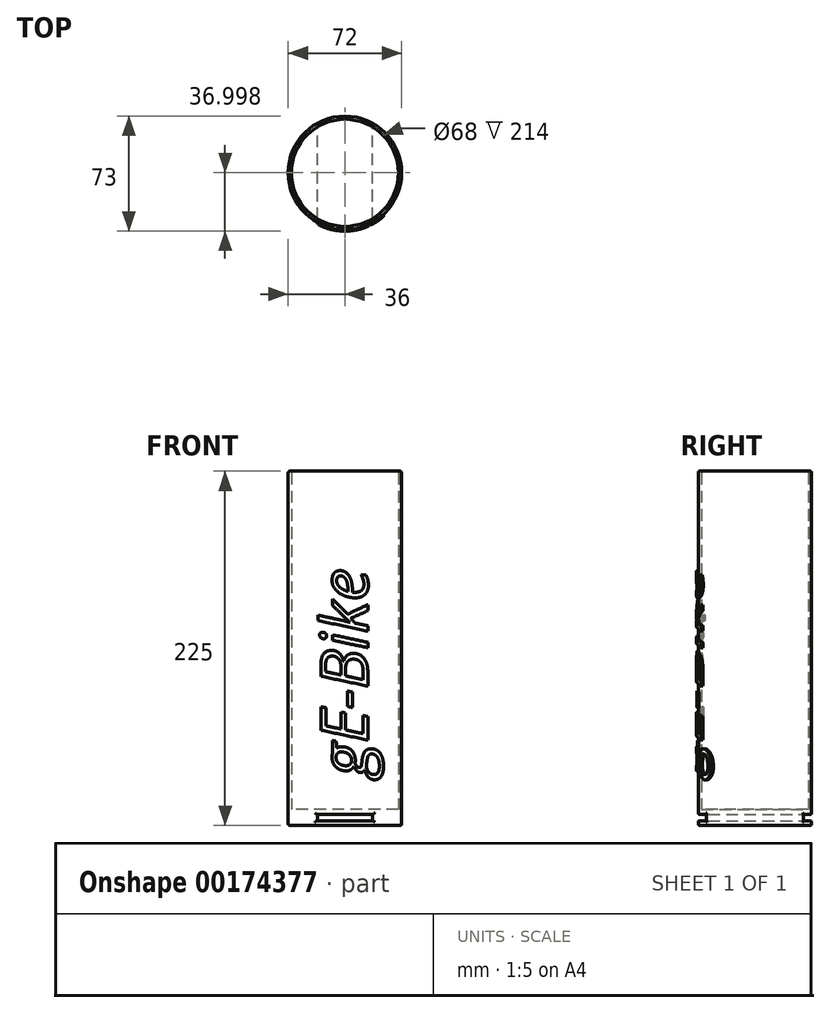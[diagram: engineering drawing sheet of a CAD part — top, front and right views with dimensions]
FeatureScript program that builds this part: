
annotation { "Feature Type Name" : "Feature", "Feature Type Description" : "" }
export const myFeature = defineFeature(function(context is Context, id is Id, definition is map)
    precondition{}
    {
        {
            var Q0;
            Q0=qCreatedBy(makeId("Top.planeOp"),FACE);
            var sketch = newSketch(context, id + "F0", { "sketchPlane" : qUnion([Q0])});
            skCircle(sketch, "E0.0", {"center": v(0, -2.8) * mm, "radius": 36 * mm});
            skLineSegment(sketch, "E1", {"start": v(0, 33.2) * mm, "end": v(0, -38.8) * mm});
            skLineSegment(sketch, "E2", {"start": v(0, -2.8) * mm, "end": v(-36, -2.8) * mm});
            skLineSegment(sketch, "E3", {"start": v(0, -2.8) * mm, "end": v(36, -2.8) * mm});
            skSolve(sketch);
        }
        {
            var Q0;
            Q0 = qSketchRegion(id + "F0", true);
            var Q1;
            Q1=makeQuery(id+"F0.imprint","IMPRINT",FACE,{"disambiguationData":[TD([[makeQuery(id+"F0.imprint","IMPRINT",EDGE,{"derivedFrom":sQuery(id+"F0.wireOp",EDGE,"E0.0")}),1.0]])]});
            extrude(context, id + "F1", {"entities" : qUnion([Q0, Q1]), "depth" : 10 * mm});
        }
        {
            var Q0;
            Q0=makeQuery(id+"F1.opExtrude","CAP_FACE",FACE,{"disambiguationData":[OSD([sQuery(id+"F0.wireOp",EDGE,"E0.0")])],"isStart":false});
            var sketch = newSketch(context, id + "F2", { "sketchPlane" : qUnion([Q0])});
            skCircle(sketch, "E4.0", {"center": v(0, -2.8) * mm, "radius": 34 * mm});
            skSolve(sketch);
        }
        {
            var Q0;
            Q0=makeQuery(id+"F2.imprint","IMPRINT",FACE,{"disambiguationData":[TD([[makeQuery(id+"F2.imprint","IMPRINT",EDGE,{"derivedFrom":sQuery(id+"F2.wireOp",EDGE,"E4.0")}),-1.0]])]});
            extrude(context, id + "F3", {"entities" : qUnion([Q0]), "operationType" : NewBodyOperationType.ADD, "depth" : 215 * mm});
        }
        {
            var Q0;
            Q0=qCreatedBy(makeId("Front.planeOp"),FACE);
            var sketch = newSketch(context, id + "F4", { "sketchPlane" : qUnion([Q0])});
            skLineSegment(sketch, "E5", {"start": v(-42.08, 0) * mm, "end": v(47.5, 0) * mm});
            skLineSegment(sketch, "E6.0", {"start": v(-17.5, 3) * mm, "end": v(17.5, 3) * mm});
            skLineSegment(sketch, "E7.0", {"start": v(-17.5, 7) * mm, "end": v(17.5, 7) * mm});
            skLineSegment(sketch, "E8.0", {"start": v(17.5, 3) * mm, "end": v(17.5, 7) * mm});
            skLineSegment(sketch, "E9.0", {"start": v(-17.5, 3) * mm, "end": v(-17.5, 7) * mm});
            skSolve(sketch);
        }
        {
            var Q0;
            Q0 = qSketchRegion(id + "F4", true);
            extrude(context, id + "F5", {"entities" : qUnion([Q0]), "operationType" : NewBodyOperationType.REMOVE, "endBound" : BoundingType.THROUGH_ALL, "depth" : 44.2 * mm, "hasSecondDirection" : true, "secondDirectionOppositeDirection" : true, "secondDirectionDepth" : 36.8 * mm});
        }
        {
            var Q0;
            Q0=makeQuery(id+"F3.opExtrude","CAP_EDGE",EDGE,{"disambiguationData":[OSD([sQuery(id+"F2.wireOp",EDGE,"E4.0")])],"isStart":false});
            var Q1;
            Q1=makeQuery(id+"F3.opExtrude","CAP_EDGE",EDGE,{"disambiguationData":[OSD([sQuery(id+"F0.wireOp",EDGE,"E0.0")])],"isStart":false});
            var Q2;
            Q2=makeQuery(id+"F1.opExtrude","CAP_EDGE",EDGE,{"disambiguationData":[OSD([sQuery(id+"F0.wireOp",EDGE,"E0.0")])],"isStart":true});
            var Q3;
            {var subQ0=sQuery(id+"F0.wireOp",EDGE,"E0.0");Q3=makeQuery(id+"F5.boolean.opBoolean","INTERSECT",EDGE,{"disambiguationData":[OD(0.0)],"derivedFrom":[makeQuery(id+"F3.boolean.opBoolean","MERGE",FACE,{"derivedFrom":[makeQuery(id+"F1.opExtrude","SWEPT_FACE",FACE,{"disambiguationData":[OSD([subQ0])]}),makeQuery(id+"F3.opExtrude","SWEPT_FACE",FACE,{"disambiguationData":[OSD([subQ0])]})]}),makeQuery(id+"F5.opExtrude","SWEPT_FACE",FACE,{"disambiguationData":[OSD([sQuery(id+"F4.wireOp",EDGE,"E7.0")])]})]});}
            var Q4;
            {var subQ0=sQuery(id+"F0.wireOp",EDGE,"E0.0");Q4=makeQuery(id+"F5.boolean.opBoolean","INTERSECT",EDGE,{"disambiguationData":[OD(0.0)],"derivedFrom":[makeQuery(id+"F3.boolean.opBoolean","MERGE",FACE,{"derivedFrom":[makeQuery(id+"F1.opExtrude","SWEPT_FACE",FACE,{"disambiguationData":[OSD([subQ0])]}),makeQuery(id+"F3.opExtrude","SWEPT_FACE",FACE,{"disambiguationData":[OSD([subQ0])]})]}),makeQuery(id+"F5.opExtrude","SWEPT_FACE",FACE,{"disambiguationData":[OSD([sQuery(id+"F4.wireOp",EDGE,"E9.0")])]})]});}
            var Q5;
            {var subQ0=sQuery(id+"F0.wireOp",EDGE,"E0.0");Q5=makeQuery(id+"F5.boolean.opBoolean","INTERSECT",EDGE,{"disambiguationData":[OD(0.0)],"derivedFrom":[makeQuery(id+"F3.boolean.opBoolean","MERGE",FACE,{"derivedFrom":[makeQuery(id+"F1.opExtrude","SWEPT_FACE",FACE,{"disambiguationData":[OSD([subQ0])]}),makeQuery(id+"F3.opExtrude","SWEPT_FACE",FACE,{"disambiguationData":[OSD([subQ0])]})]}),makeQuery(id+"F5.opExtrude","SWEPT_FACE",FACE,{"disambiguationData":[OSD([sQuery(id+"F4.wireOp",EDGE,"E6.0")])]})]});}
            var Q6;
            {var subQ0=sQuery(id+"F0.wireOp",EDGE,"E0.0");Q6=makeQuery(id+"F5.boolean.opBoolean","INTERSECT",EDGE,{"disambiguationData":[OD(0.0)],"derivedFrom":[makeQuery(id+"F3.boolean.opBoolean","MERGE",FACE,{"derivedFrom":[makeQuery(id+"F1.opExtrude","SWEPT_FACE",FACE,{"disambiguationData":[OSD([subQ0])]}),makeQuery(id+"F3.opExtrude","SWEPT_FACE",FACE,{"disambiguationData":[OSD([subQ0])]})]}),makeQuery(id+"F5.opExtrude","SWEPT_FACE",FACE,{"disambiguationData":[OSD([sQuery(id+"F4.wireOp",EDGE,"E8.0")])]})]});}
            var Q7;
            {var subQ0=sQuery(id+"F0.wireOp",EDGE,"E0.0");Q7=makeQuery(id+"F5.boolean.opBoolean","INTERSECT",EDGE,{"disambiguationData":[OD(1.0)],"derivedFrom":[makeQuery(id+"F3.boolean.opBoolean","MERGE",FACE,{"derivedFrom":[makeQuery(id+"F1.opExtrude","SWEPT_FACE",FACE,{"disambiguationData":[OSD([subQ0])]}),makeQuery(id+"F3.opExtrude","SWEPT_FACE",FACE,{"disambiguationData":[OSD([subQ0])]})]}),makeQuery(id+"F5.opExtrude","SWEPT_FACE",FACE,{"disambiguationData":[OSD([sQuery(id+"F4.wireOp",EDGE,"E7.0")])]})]});}
            var Q8;
            {var subQ0=sQuery(id+"F0.wireOp",EDGE,"E0.0");Q8=makeQuery(id+"F5.boolean.opBoolean","INTERSECT",EDGE,{"disambiguationData":[OD(1.0)],"derivedFrom":[makeQuery(id+"F3.boolean.opBoolean","MERGE",FACE,{"derivedFrom":[makeQuery(id+"F1.opExtrude","SWEPT_FACE",FACE,{"disambiguationData":[OSD([subQ0])]}),makeQuery(id+"F3.opExtrude","SWEPT_FACE",FACE,{"disambiguationData":[OSD([subQ0])]})]}),makeQuery(id+"F5.opExtrude","SWEPT_FACE",FACE,{"disambiguationData":[OSD([sQuery(id+"F4.wireOp",EDGE,"E9.0")])]})]});}
            var Q9;
            {var subQ0=sQuery(id+"F0.wireOp",EDGE,"E0.0");Q9=makeQuery(id+"F5.boolean.opBoolean","INTERSECT",EDGE,{"disambiguationData":[OD(1.0)],"derivedFrom":[makeQuery(id+"F3.boolean.opBoolean","MERGE",FACE,{"derivedFrom":[makeQuery(id+"F1.opExtrude","SWEPT_FACE",FACE,{"disambiguationData":[OSD([subQ0])]}),makeQuery(id+"F3.opExtrude","SWEPT_FACE",FACE,{"disambiguationData":[OSD([subQ0])]})]}),makeQuery(id+"F5.opExtrude","SWEPT_FACE",FACE,{"disambiguationData":[OSD([sQuery(id+"F4.wireOp",EDGE,"E6.0")])]})]});}
            var Q10;
            {var subQ0=sQuery(id+"F0.wireOp",EDGE,"E0.0");Q10=makeQuery(id+"F5.boolean.opBoolean","INTERSECT",EDGE,{"disambiguationData":[OD(1.0)],"derivedFrom":[makeQuery(id+"F3.boolean.opBoolean","MERGE",FACE,{"derivedFrom":[makeQuery(id+"F1.opExtrude","SWEPT_FACE",FACE,{"disambiguationData":[OSD([subQ0])]}),makeQuery(id+"F3.opExtrude","SWEPT_FACE",FACE,{"disambiguationData":[OSD([subQ0])]})]}),makeQuery(id+"F5.opExtrude","SWEPT_FACE",FACE,{"disambiguationData":[OSD([sQuery(id+"F4.wireOp",EDGE,"E8.0")])]})]});}
            fillet(context, id + "F6", {"entities" : qUnion([Q0, Q1, Q2, Q3, Q4, Q5, Q6, Q7, Q8, Q9, Q10]), "radius" : 1 * mm, "tangentPropagation" : true, "allowEdgeOverflow" : false});
        }
        {
            var Q0;
            Q0=qCreatedBy(makeId("Front.planeOp"),FACE);
            cPlane(context, id + "F7", {"entities" : qUnion([Q0]), "cplaneType" : CPlaneType.OFFSET, "offset" : 40 * mm, "width" : 150 * mm, "height" : 150 * mm});
        }
        {
            var Q0;
            Q0=qCreatedBy(id+"F7.planeOp",FACE);
            var sketch = newSketch(context, id + "F8", { "sketchPlane" : qUnion([Q0])});
            skText(sketch, "E10", { "text": "gE-Bike", "fontName": "OpenSans-Italic.ttf"});
            const initialGuessF8  = {"E10": [0.01453, 0.03153, 0, 1, 0.03]};
            skSetInitialGuess(sketch, initialGuessF8);
            skSolve(sketch);
        }
        {
            var Q0;
            Q0 = qSketchRegion(id + "F8", true);
            extrude(context, id + "F9", {"entities" : qUnion([Q0]), "operationType" : NewBodyOperationType.ADD, "endBound" : BoundingType.UP_TO_NEXT, "oppositeDirection" : true, "depth" : 25.7 * mm});
        }
        {
            var Q0;
            Q0=makeQuery(id+"F1.opExtrude","CAP_FACE",FACE,{"disambiguationData":[OSD([sQuery(id+"F0.wireOp",EDGE,"E0.0")])],"isStart":true});
            var sketch = newSketch(context, id + "F10", { "sketchPlane" : qUnion([Q0])});
            skCircle(sketch, "E11.0", {"center": v(0, 2.8) * mm, "radius": 37 * mm});
            skCircle(sketch, "E12", {"center": v(0, 2.8) * mm, "radius": 36 * mm});
            skCircle(sketch, "E13.0", {"center": v(0, 2.8) * mm, "radius": 52 * mm});
            skSolve(sketch);
        }
        {
            var Q0;
            Q0=makeQuery(id+"F10.imprint","IMPRINT",FACE,{"disambiguationData":[TD([[makeQuery(id+"F10.imprint","IMPRINT",EDGE,{"derivedFrom":sQuery(id+"F10.wireOp",EDGE,"E11.0")}),-1.0]])]});
            extrude(context, id + "F11", {"entities" : qUnion([Q0]), "operationType" : NewBodyOperationType.REMOVE, "oppositeDirection" : true, "depth" : 193 * mm});
        }
    });
